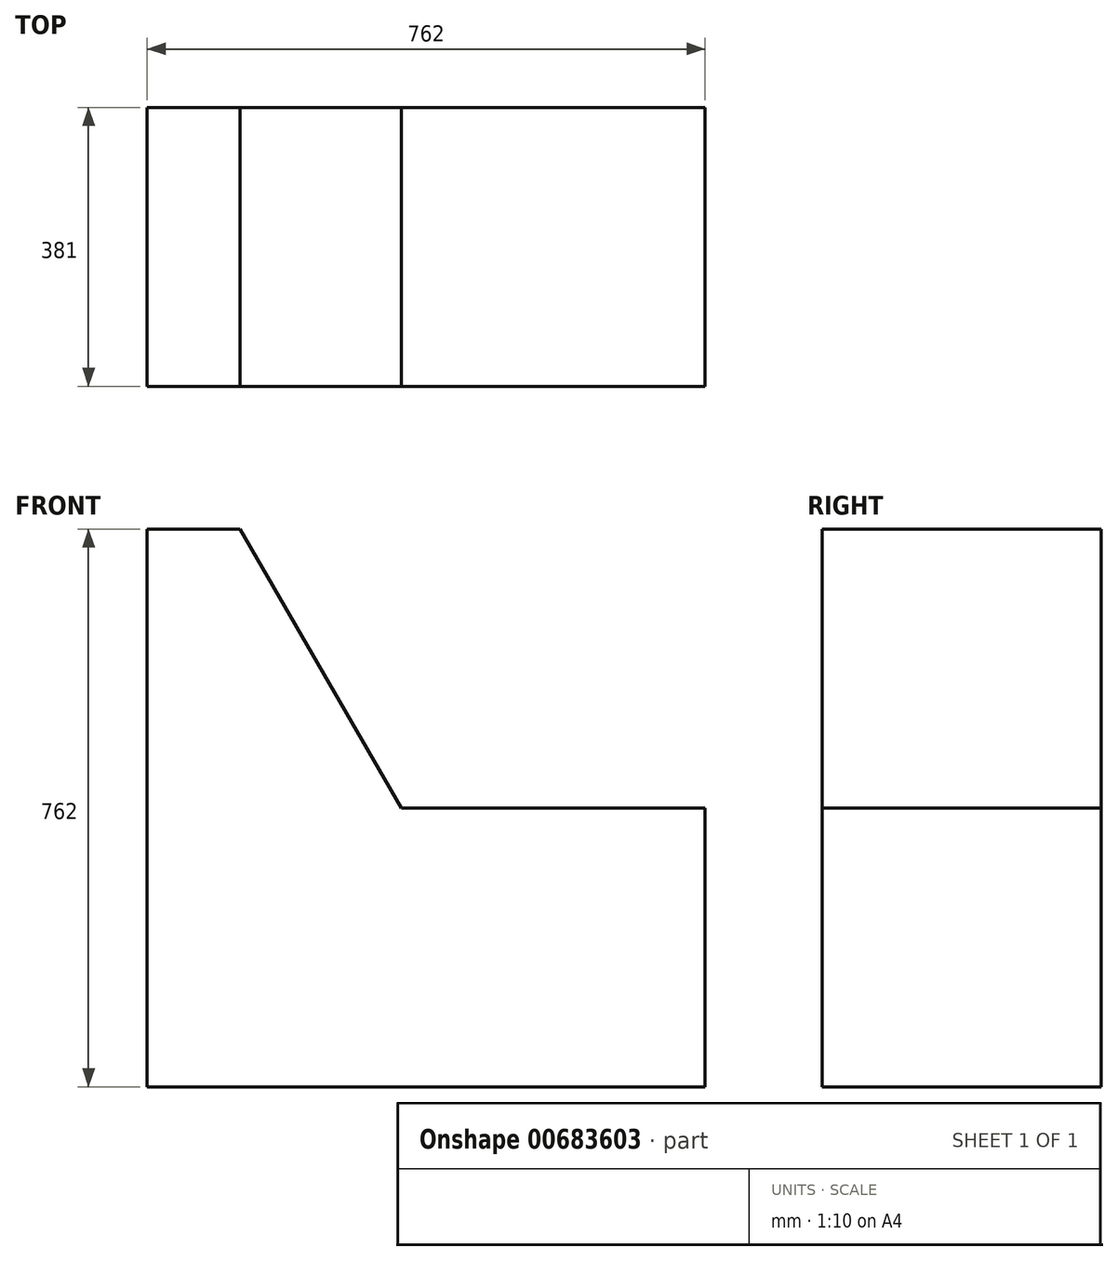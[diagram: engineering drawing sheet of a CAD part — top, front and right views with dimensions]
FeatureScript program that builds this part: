
annotation { "Feature Type Name" : "Feature", "Feature Type Description" : "" }
export const myFeature = defineFeature(function(context is Context, id is Id, definition is map)
    precondition{}
    {
        {
            var Q0;
            Q0=qCreatedBy(makeId("Front.planeOp"),FACE);
            var sketch = newSketch(context, id + "F0", { "sketchPlane" : qUnion([Q0])});
            skLineSegment(sketch, "E0", {"start": v(-889, 762) * mm, "end": v(-889, 0) * mm});
            skLineSegment(sketch, "E1", {"start": v(-889, 0) * mm, "end": v(-127, 0) * mm});
            skLineSegment(sketch, "E2", {"start": v(-127, 0) * mm, "end": v(-127, 381) * mm});
            skLineSegment(sketch, "E3", {"start": v(-889, 762) * mm, "end": v(-762, 762) * mm});
            skLineSegment(sketch, "E4", {"start": v(-762, 762) * mm, "end": v(-542.03, 381) * mm});
            skLineSegment(sketch, "E5", {"start": v(-542.03, 381) * mm, "end": v(-127, 381) * mm});
            skSolve(sketch);
        }
        {
            var Q0;
            Q0=makeQuery(id+"F0.imprint","IMPRINT",FACE,{"disambiguationData":[TD([[makeQuery(id+"F0.imprint","IMPRINT",EDGE,{"derivedFrom":sQuery(id+"F0.wireOp",EDGE,"E0")}),1.0]])]});
            extrude(context, id + "F1", {"entities" : qUnion([Q0]), "depth" : 381 * mm, "offsetDistance" : 25.4 * mm});
        }
    });
